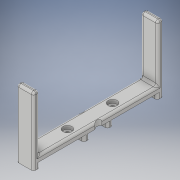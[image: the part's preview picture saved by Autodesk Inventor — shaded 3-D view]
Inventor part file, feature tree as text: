
AUTODESK INVENTOR PART (.ipt)
format: ipt  version: 2019.4 (Build 234330000, 330)  size: 279,552 bytes
history: native  units: mm
features: sketch x8, extrude x7, fillet x6
ambient origin geometry x8: Origin, YZ Plane, XZ Plane, XY Plane, X Axis, Y Axis, Z Axis, Center Point
bodies: Solid1 (feature_tree)
feature tree (21):
  extrude  "Extrusion1"  TaperAngle=90.0deg  [1 undecoded]
  extrude  "Extrusion2"  Depth=5.0mm TaperAngle=0.0deg
  extrude  "Extrusion3"  Depth=20.0mm
  extrude  "Extrusion4"  Depth=3.25mm
  fillet  "Fillet1"  Radius=5.0mm
  fillet  "Fillet2"  Radius=8.0mm
  fillet  "Fillet3"  Radius=8.0mm
  sketch  "Sketch5"  dims[d15=15.0mm d16=5.0mm]
  fillet  "Fillet4"  Radius=3.0mm
  extrude  "Extrusion5"  Depth=5.0mm
  extrude  "Extrusion6"  Depth=2.0mm
  fillet  "Fillet5"  Radius=50.0mm
  fillet  "Fillet6"  Radius=2.0mm
  extrude  "Extrusion7"  Depth=2.0mm
  sketch  "Sketch1"  dims[d0=115.0mm d1=90.0deg]
  sketch  "Sketch2"  dims[d2=15.0mm d3=5.0mm d4=0.0mm]
  sketch  "Sketch3"  dims[d5=20.0mm d6=20.0mm]
  sketch  "Sketch4"  dims[d7=3.25mm d8=3.25mm d9=5.0mm d10=0.0mm d11=8.0mm d12=8.0mm d13=3.0mm d14=0.0mm]
  sketch  "Sketch6"  dims[d17=15.0mm d18=5.0mm d19=50.0mm d20=0.0mm d21=2.0mm]
  sketch  "Sketch7"  dims[d22=2.0mm d23=2.0mm]
  sketch  "Sketch8"  dims[d24=2.0mm d25=8.0mm d26=8.0mm d27=5.0mm d28=8.0mm d29=5.0mm d30=8.0mm d31=39.0mm d32=5.5mm d33=39.0mm d34=15.0mm d35=180.0deg d36=5.5mm d37=5.0mm d38=0.0mm d39=8.0mm d40=15.0mm d41=180.0deg d42=5.0mm d43=5.0mm d44=0.0mm d45=2.0mm d46=2.0mm d47=10.0mm d48=10.0mm d49=8.0mm d50=8.0mm d51=5.0mm d52=0.0mm]
note: 1 required parameter value undecoded (feature->parameter linkage not recoverable at this tier; creation-order binding heuristic only, values carry confidence <= 0.55)
